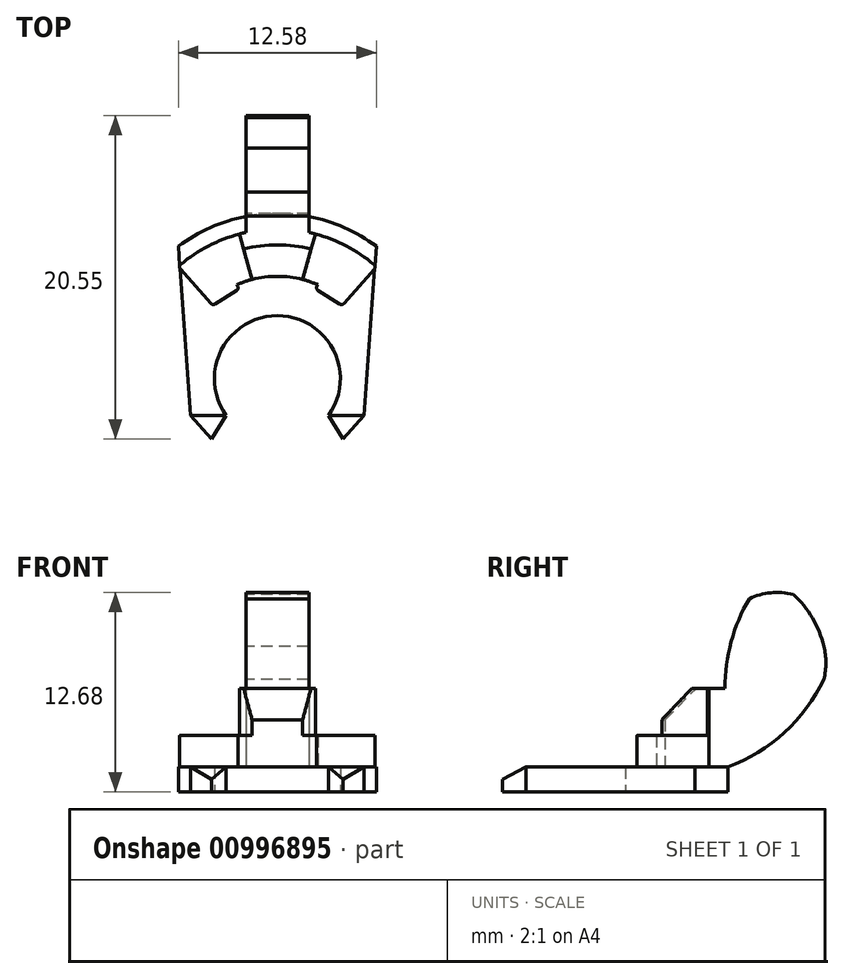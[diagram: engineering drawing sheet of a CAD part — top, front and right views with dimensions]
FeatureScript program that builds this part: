
annotation { "Feature Type Name" : "Feature", "Feature Type Description" : "" }
export const myFeature = defineFeature(function(context is Context, id is Id, definition is map)
    precondition{}
    {
        {
            var Q0;
            Q0=qCreatedBy(makeId("Top.planeOp"),FACE);
            var sketch = newSketch(context, id + "F0", { "sketchPlane" : qUnion([Q0])});
            skLineSegment(sketch, "E0", {"start": v(-7.13, -2.33) * mm, "end": v(-5.5, -2.33) * mm, "construction": true});
            skLineSegment(sketch, "E1", {"start": v(-3.25, -2.33) * mm, "end": v(3.25, -2.33) * mm, "construction": true});
            skLineSegment(sketch, "E2", {"start": v(3.25, -2.33) * mm, "end": v(5.5, -2.33) * mm, "construction": true});
            skArc(sketch, "E3", {"start": v(-7.13, -2.33) * mm, "mid": v(0, -7.5) * mm, "end": v(7.13, -2.33) * mm, "construction": true});
            skArc(sketch, "E4", {"start": v(7.13, -2.33) * mm, "mid": v(7.4, 1.22) * mm, "end": v(6, 4.5) * mm, "construction": true});
            skArc(sketch, "E5", {"start": v(3.25, -2.33) * mm, "mid": v(0, 4) * mm, "end": v(-3.25, -2.33) * mm});
            skArc(sketch, "E6", {"start": v(-3.25, -2.33) * mm, "mid": v(0, -4) * mm, "end": v(3.25, -2.33) * mm, "construction": true});
            skLineSegment(sketch, "E7", {"start": v(-6, 4.5) * mm, "end": v(6, 4.5) * mm, "construction": true});
            skArc(sketch, "E8", {"start": v(6, 4.5) * mm, "mid": v(0, 7.5) * mm, "end": v(-6, 4.5) * mm, "construction": true});
            skArc(sketch, "E9", {"start": v(-6, 4.5) * mm, "mid": v(-7.4, 1.22) * mm, "end": v(-7.13, -2.33) * mm, "construction": true});
            skLineSegment(sketch, "E10", {"start": v(-6.29, 8.41) * mm, "end": v(-5.5, -2.33) * mm});
            skLineSegment(sketch, "E11", {"start": v(6.29, 8.41) * mm, "end": v(5.5, -2.33) * mm});
            skLineSegment(sketch, "E12", {"start": v(-5.5, -2.33) * mm, "end": v(-3.25, -2.33) * mm, "construction": true});
            skLineSegment(sketch, "E13", {"start": v(5.5, -2.33) * mm, "end": v(7.13, -2.33) * mm, "construction": true});
            skLineSegment(sketch, "E14", {"start": v(-5.5, -2.33) * mm, "end": v(-4.18, -3.83) * mm});
            skLineSegment(sketch, "E15", {"start": v(-4.18, -3.83) * mm, "end": v(-3.25, -2.33) * mm});
            skLineSegment(sketch, "E16", {"start": v(3.25, -2.33) * mm, "end": v(4.18, -3.83) * mm});
            skLineSegment(sketch, "E17", {"start": v(4.18, -3.83) * mm, "end": v(5.5, -2.33) * mm});
            skArc(sketch, "E18", {"start": v(-6.29, 8.41) * mm, "mid": v(0, 10.5) * mm, "end": v(6.29, 8.41) * mm});
            skPoint(sketch, "E19", {"position": v(0, 10.5) * mm});
            skPoint(sketch, "E20", {"position": v(0, 7.5) * mm});
            skSolve(sketch);
        }
        {
            var Q0;
            Q0=qSketchRegion(id+"F0",true);
            extrude(context, id + "F1", {"entities" : qUnion([Q0]), "offsetDistance" : 25 * mm, "depth" : 1.2 * mm, "hasSecondDirection" : true, "secondDirectionOppositeDirection" : true, "secondDirectionDepth" : 0.4 * mm});
        }
        {
            var Q0;
            Q0=qCreatedBy(makeId("Right.planeOp"),FACE);
            var sketch = newSketch(context, id + "F2", { "sketchPlane" : qUnion([Q0])});
            skPoint(sketch, "E21.0", {"position": v(-2.33, 1.2) * mm});
            skLineSegment(sketch, "E22", {"start": v(-2.33, 1.2) * mm, "end": v(-3.83, 0.4) * mm});
            skLineSegment(sketch, "E23", {"start": v(-3.83, 0.4) * mm, "end": v(-3.83, 1.2) * mm});
            skLineSegment(sketch, "E24", {"start": v(-2.33, 1.2) * mm, "end": v(-3.83, 1.2) * mm});
            skSolve(sketch);
        }
        {
            var Q0;
            Q0=qSketchRegion(id+"F2",true);
            extrude(context, id + "F3", {"entities" : qUnion([Q0]), "operationType" : NewBodyOperationType.REMOVE, "endBound" : BoundingType.SYMMETRIC, "oppositeDirection" : true, "depth" : 25 * mm});
        }
        {
            var Q0;
            Q0=makeQuery(id+"F1.opExtrude","CAP_FACE",FACE,{"disambiguationData":[OSD([sQuery(id+"F0.wireOp",EDGE,"E5"),sQuery(id+"F0.wireOp",EDGE,"E10"),sQuery(id+"F0.wireOp",EDGE,"E11"),sQuery(id+"F0.wireOp",EDGE,"E14"),sQuery(id+"F0.wireOp",EDGE,"E15"),sQuery(id+"F0.wireOp",EDGE,"E16"),sQuery(id+"F0.wireOp",EDGE,"E17"),sQuery(id+"F0.wireOp",EDGE,"E18")])],"isStart":false});
            var sketch = newSketch(context, id + "F4", { "sketchPlane" : qUnion([Q0])});
            skArc(sketch, "E25.0", {"start": v(0, 9.5) * mm, "mid": v(-3.27, 8.92) * mm, "end": v(-6.14, 7.25) * mm});
            skArc(sketch, "E26.0", {"start": v(0, 6.5) * mm, "mid": v(-1.31, 6.37) * mm, "end": v(-2.58, 5.97) * mm});
            skPoint(sketch, "E27", {"position": v(0, 9.5) * mm});
            skPoint(sketch, "E28", {"position": v(0, 6.5) * mm});
            skLineSegment(sketch, "E29", {"start": v(-6.3, 7.12) * mm, "end": v(-6.71, 6.74) * mm, "construction": true});
            skLineSegment(sketch, "E30", {"start": v(-6.16, 6.97) * mm, "end": v(-4.3, 4.87) * mm});
            skLineSegment(sketch, "E31", {"start": v(-4.3, 4.87) * mm, "end": v(-4.22, 4.77) * mm});
            skLineSegment(sketch, "E32", {"start": v(-3.96, 4.74) * mm, "end": v(-2.58, 5.6) * mm});
            skLineSegment(sketch, "E33", {"start": v(-2.52, 5.88) * mm, "end": v(-2.58, 5.97) * mm});
            skLineSegment(sketch, "E34", {"start": v(0, 9.5) * mm, "end": v(0, 6.5) * mm, "construction": true});
            skPoint(sketch, "E35.start.orphan", {"position": v(3.7, 8.75) * mm});
            skPoint(sketch, "E36.visualSharp", {"position": v(-6.3, 7.12) * mm});
            skArc(sketch, "E36.filletArc", {"start": v(-6.14, 7.25) * mm, "mid": v(-6.2, 7.11) * mm, "end": v(-6.16, 6.97) * mm});
            skPoint(sketch, "E37.visualSharp", {"position": v(-4.1, 4.65) * mm});
            skArc(sketch, "E37.filletArc", {"start": v(-4.22, 4.77) * mm, "mid": v(-4.1, 4.7) * mm, "end": v(-3.96, 4.74) * mm});
            skPoint(sketch, "E38.visualSharp", {"position": v(-2.41, 5.71) * mm});
            skArc(sketch, "E38.filletArc", {"start": v(-2.58, 5.6) * mm, "mid": v(-2.5, 5.73) * mm, "end": v(-2.52, 5.88) * mm});
            skLineSegment(sketch, "E39.MirrorCS", {"start": v(4.3, 4.87) * mm, "end": v(4.22, 4.77) * mm});
            skArc(sketch, "E40.MirrorCS", {"start": v(4.22, 4.77) * mm, "mid": v(4.1, 4.7) * mm, "end": v(3.96, 4.74) * mm});
            skLineSegment(sketch, "E41.MirrorCS", {"start": v(3.96, 4.74) * mm, "end": v(2.58, 5.6) * mm});
            skPoint(sketch, "E42.MirrorP", {"position": v(4.1, 4.65) * mm});
            skLineSegment(sketch, "E43.MirrorCS", {"start": v(6.16, 6.97) * mm, "end": v(4.3, 4.87) * mm});
            skArc(sketch, "E44.MirrorCS", {"start": v(0, 9.5) * mm, "mid": v(3.27, 8.92) * mm, "end": v(6.14, 7.25) * mm});
            skLineSegment(sketch, "E45.MirrorCS", {"start": v(2.52, 5.88) * mm, "end": v(2.58, 5.97) * mm});
            skArc(sketch, "E46.MirrorCS", {"start": v(2.58, 5.6) * mm, "mid": v(2.5, 5.73) * mm, "end": v(2.52, 5.88) * mm});
            skArc(sketch, "E47.MirrorCS", {"start": v(6.14, 7.25) * mm, "mid": v(6.2, 7.11) * mm, "end": v(6.16, 6.97) * mm});
            skArc(sketch, "E48.MirrorCS", {"start": v(0, 6.5) * mm, "mid": v(1.31, 6.37) * mm, "end": v(2.58, 5.97) * mm});
            skPoint(sketch, "E49.MirrorP", {"position": v(6.3, 7.12) * mm});
            skPoint(sketch, "E50.MirrorP", {"position": v(2.41, 5.71) * mm});
            skLineSegment(sketch, "E51", {"start": v(0, 6.5) * mm, "end": v(0, 9.5) * mm});
            skLineSegment(sketch, "E52", {"start": v(1.6, 6.3) * mm, "end": v(2.41, 9.19) * mm});
            skLineSegment(sketch, "E53.MirrorCS", {"start": v(-1.6, 6.3) * mm, "end": v(-2.41, 9.19) * mm});
            skPoint(sketch, "E54.oppositeSnap0", {"position": v(0, 10.5) * mm});
            skLineSegment(sketch, "E54.top", {"start": v(-2, 10.31) * mm, "end": v(0, 10.31) * mm});
            skLineSegment(sketch, "E54.left", {"start": v(-2, 9.29) * mm, "end": v(-2, 10.31) * mm});
            skLineSegment(sketch, "E54.right", {"start": v(0, 9.49) * mm, "end": v(0, 10.31) * mm});
            skLineSegment(sketch, "E55.MirrorCS", {"start": v(2, 9.29) * mm, "end": v(2, 10.31) * mm});
            skLineSegment(sketch, "E56.MirrorCS", {"start": v(2, 10.31) * mm, "end": v(0, 10.31) * mm});
            skSolve(sketch);
        }
        {
            var Q0;
            Q0=qSketchRegion(id+"F4",true);
            extrude(context, id + "F5", {"entities" : qUnion([Q0]), "operationType" : NewBodyOperationType.ADD, "offsetDistance" : 25 * mm, "depth" : 2 * mm});
        }
        {
            var Q0;
            {var subQ0=sQuery(id+"F4.wireOp",EDGE,"E51");Q0=makeQuery(id+"F4.imprint","IMPRINT",FACE,{"disambiguationData":[TD([[makeQuery(id+"F4.imprint","IMPRINT",EDGE,{"derivedFrom":subQ0}),-1.0]])]});}
            var Q1;
            {var subQ0=sQuery(id+"F4.wireOp",EDGE,"E51");Q1=makeQuery(id+"F4.imprint","IMPRINT",FACE,{"disambiguationData":[TD([[makeQuery(id+"F4.imprint","IMPRINT",EDGE,{"derivedFrom":subQ0}),1.0]])]});}
            extrude(context, id + "F6", {"entities" : qUnion([Q0, Q1]), "operationType" : NewBodyOperationType.ADD, "depth" : 5 * mm, "offsetDistance" : 25 * mm});
        }
        {
            var Q0;
            Q0=makeQuery(id+"F6.opExtrude","CAP_EDGE",EDGE,{"disambiguationData":[OSD([sQuery(id+"F4.wireOp",EDGE,"E26.0"),sQuery(id+"F4.wireOp",EDGE,"E48.MirrorCS")])],"isStart":false});
            chamfer(context, id + "F7", {"entities" : qUnion([Q0]), "width" : 2 * mm, "tangentPropagation" : true});
        }
        {
            var Q0;
            {var subQ3=sQuery(id+"F4.wireOp",EDGE,"E55.MirrorCS");Q0=makeQuery(id+"F4.imprint","IMPRINT",FACE,{"disambiguationData":[TD([[makeQuery(id+"F4.imprint","IMPRINT",EDGE,{"derivedFrom":subQ3}),1.0]])]});}
            var Q1;
            {var subQ4=sQuery(id+"F4.wireOp",EDGE,"E54.top");Q1=makeQuery(id+"F4.imprint","IMPRINT",FACE,{"disambiguationData":[TD([[makeQuery(id+"F4.imprint","IMPRINT",EDGE,{"derivedFrom":subQ4}),-1.0]])]});}
            var Q2;
            Q2=makeQuery(id+"F6.opExtrude","CAP_FACE",FACE,{"disambiguationData":[OSD([sQuery(id+"F4.wireOp",EDGE,"E25.0"),sQuery(id+"F4.wireOp",EDGE,"E26.0"),sQuery(id+"F4.wireOp",EDGE,"E44.MirrorCS"),sQuery(id+"F4.wireOp",EDGE,"E48.MirrorCS"),sQuery(id+"F4.wireOp",EDGE,"E52"),sQuery(id+"F4.wireOp",EDGE,"E53.MirrorCS")])],"isStart":false});
            var Q3;
            Q3=makeQuery(id+"F1.opExtrude","SWEPT_BODY",BODY,{"disambiguationData":[OSD([sQuery(id+"F0.wireOp",EDGE,"E5"),sQuery(id+"F0.wireOp",EDGE,"E10"),sQuery(id+"F0.wireOp",EDGE,"E11"),sQuery(id+"F0.wireOp",EDGE,"E14"),sQuery(id+"F0.wireOp",EDGE,"E15"),sQuery(id+"F0.wireOp",EDGE,"E16"),sQuery(id+"F0.wireOp",EDGE,"E17"),sQuery(id+"F0.wireOp",EDGE,"E18")])]});
            extrude(context, id + "F8", {"entities" : qUnion([Q0, Q1]), "operationType" : NewBodyOperationType.ADD, "endBound" : BoundingType.UP_TO_SURFACE, "depth" : 25 * mm, "endBoundEntityFace" : qUnion([Q2]), "endBoundEntityBody" : qUnion([Q3]), "offsetDistance" : 25 * mm});
        }
        {
            var Q0;
            {var subQ0=sQuery(id+"F4.wireOp",EDGE,"E54.left");Q0=makeQuery(id+"F8.boolean.opBoolean","MERGE",FACE,{"derivedFrom":[makeQuery(id+"F5.opExtrude","SWEPT_FACE",FACE,{"disambiguationData":[OSD([subQ0])]}),makeQuery(id+"F8.opExtrude","SWEPT_FACE",FACE,{"disambiguationData":[OSD([subQ0])]})]});}
            var sketch = newSketch(context, id + "F9", { "sketchPlane" : qUnion([Q0])});
            skLineSegment(sketch, "E57", {"start": v(-10.31, 1.2) * mm, "end": v(-10.5, 1.2) * mm});
            skArc(sketch, "E58", {"start": v(-16.58, 6.76) * mm, "mid": v(-14.09, 3.38) * mm, "end": v(-10.5, 1.2) * mm});
            skArc(sketch, "E59", {"start": v(-16.58, 8.86) * mm, "mid": v(-16.72, 7.8) * mm, "end": v(-16.58, 6.76) * mm});
            skArc(sketch, "E60", {"start": v(-14.64, 12.15) * mm, "mid": v(-15.87, 10.65) * mm, "end": v(-16.58, 8.86) * mm});
            skArc(sketch, "E61", {"start": v(-10.31, 6.2) * mm, "mid": v(-10.7, 9.14) * mm, "end": v(-11.85, 11.88) * mm});
            skArc(sketch, "E62", {"start": v(-11.85, 11.88) * mm, "mid": v(-13.22, 12.26) * mm, "end": v(-14.64, 12.15) * mm});
            skSolve(sketch);
        }
        {
            var Q0;
            Q0=makeQuery(id+"F9.imprint","IMPRINT",FACE,{"disambiguationData":[TD([[makeQuery(id+"F9.imprint","IMPRINT",EDGE,{"derivedFrom":sQuery(id+"F9.wireOp",EDGE,"LY1qM96g-48ux-B85P-QWtM-bPvA0SawryY8")}),-1.0]])]});
            var Q1;
            Q1=makeQuery(id+"F9.imprint","IMPRINT",FACE,{"disambiguationData":[TD([[makeQuery(id+"F9.imprint","IMPRINT",EDGE,{"derivedFrom":sQuery(id+"F9.wireOp",EDGE,"E57")}),-1.0]])]});
            extrude(context, id + "F10", {"entities" : qUnion([Q0, Q1]), "operationType" : NewBodyOperationType.ADD, "oppositeDirection" : true, "depth" : 4 * mm, "offsetDistance" : 25 * mm});
        }
        {
            var Q0;
            {var subQ5=sQuery(id+"F4.wireOp",EDGE,"E44.MirrorCS");var subQ7=sQuery(id+"F4.wireOp",EDGE,"E55.MirrorCS");var subQ8=makeQuery(id+"F4.imprint","INTERSECT",VERTEX,{"derivedFrom":[subQ5,subQ7]});Q0=makeQuery(id+"F4.imprint","IMPRINT",FACE,{"disambiguationData":[TD([[makeQuery(id+"F4.imprint","IMPRINT",EDGE,{"disambiguationData":[TD([[subQ8,-1.0]])],"derivedFrom":subQ7}),1.0]])]});}
            var Q1;
            {var subQ1=sQuery(id+"F4.wireOp",EDGE,"E25.0");var subQ5=sQuery(id+"F4.wireOp",EDGE,"E54.left");var subQ6=makeQuery(id+"F4.imprint","INTERSECT",VERTEX,{"derivedFrom":[subQ1,subQ5]});Q1=makeQuery(id+"F4.imprint","IMPRINT",FACE,{"disambiguationData":[TD([[makeQuery(id+"F4.imprint","IMPRINT",EDGE,{"disambiguationData":[TD([[subQ6,-1.0]])],"derivedFrom":subQ5}),-1.0]])]});}
            var Q2;
            Q2=makeQuery(id+"F6.opExtrude","CAP_FACE",FACE,{"disambiguationData":[OSD([sQuery(id+"F4.wireOp",EDGE,"E25.0"),sQuery(id+"F4.wireOp",EDGE,"E26.0"),sQuery(id+"F4.wireOp",EDGE,"E44.MirrorCS"),sQuery(id+"F4.wireOp",EDGE,"E48.MirrorCS"),sQuery(id+"F4.wireOp",EDGE,"E52"),sQuery(id+"F4.wireOp",EDGE,"E53.MirrorCS")])],"isStart":false});
            extrude(context, id + "F11", {"entities" : qUnion([Q0, Q1]), "operationType" : NewBodyOperationType.ADD, "endBound" : BoundingType.UP_TO_SURFACE, "depth" : 25 * mm, "endBoundEntityFace" : qUnion([Q2]), "offsetDistance" : 25 * mm});
        }
    });
